# Revit family: Hager-Univers-IP65-D300-H1150-Cl.II-encl-NoHosted-CH-it
name_source: partatom
category: Electrical Equipment
units: mm (PartAtom-declared; Revit-internal decimal feet)

## family parameters
Always vertical = Yes
Cut with Voids When Loaded = No
Panel Configuration = Two Columns, Circuits Across
Part Type = Panelboard
Room Calculation Point = No
Round Connector Dimension = Use Diameter
Shared = No
Work Plane-Based = Yes

## types (6) — shared parameters
Default Elevation = 1219 mm
EF000003 - Tipo di montaggio = EV000384 - A parete
EF000007 - colore = EV000270 - grigio
EF000040 - Altezza = 1150 mm
EF000049 - profondità = 300 mm  [stored 0.984252 ft]
EF000116 - numero RAL = 7035
EF000118 - con piastra di montaggio = No
EF000266 - numero di file = 7
EF001088 - possibilità di applicazione = No
EF001131 - profondità interna = 300 mm  [stored 0.984252 ft]
EF001596 - Attacco Lampada = EV000139 - plastica
EF001613 - Integrità del circuito = EV000494 - senza
EF003532 - adatto per uso esterno = Yes
EF004293 - resistenza agli urti = EV008784 - IK10
EF004464 - tipo di porta = EV002646 - singolo
EF005474 - grado di protezione (IP) = EV006421 - IP65
EF006244 - coperchio/porta trasparente = No
EF006306 - con serratura = Yes
EF007800 - adatto per parafulmine = Yes
EF009170 - spessore materiale scatola = 2 mm  [stored 0.00656168 ft]
EF009171 - spessore materiale porta/coperchio = 2 mm  [stored 0.00656168 ft]
EF009212 - esecuzione coperchio = EV000116 - chiuso
EF015940 - Coprire con rilascio di sovrapressione = No
HG000002 - Con porta = Yes
HG000003 - Gamma = Univers
HG000006 - Ad incasso = No
HG000009 - Porta doppia a battente = No
HG000010 - Porte asimmetriche = No
HG000023 - Custodia a doppia sezione = No
HG000024 - Altezza della sezione inferiore = 600 mm
HG000026 - A pavimento = No
Manufacturer = Hager
Type Comments = Univers
zero-valued in all types: EF000218 - profondità di incasso, EF009554 - numero delle aperture per la piastra della flangia, HG000027 - Altezza dello zoccolo

## per-type parameters (varying)
| type | EF000008 - Larghezza | EF000339 - tipo di copertura | EF000437 - numero di ingressi per conduttori | EF002950 - Numero moduli DIN | EF004427 - numero di moduli | EF008873 - corrente nominale (In) | HG000004 - Codice produttore |
| A parete IP65 L1100 A1150 P300  - FL74S | 1100 mm | EV004216 - porta | 0 | 48 | 336 | 630 A | FL74S |
| A parete IP65 L1100 A1150 P300  - FL74SP | 1100 mm | EV004216 - porta | 0 | 48 | 336 | 630 A | FL74SP |
| A parete IP65 L600 A1150 P300  - FL72S | 600 mm | EV001012 - coperchio | 2 | 24 | 168 | 400 A | FL72S |
| A parete IP65 L600 A1150 P300  - FL72SP | 600 mm | EV001012 - coperchio | 2 | 24 | 168 | 400 A | FL72SP |
| A parete IP65 L850 A1150 P300  - FL73S | 850 mm  [stored 2.78871 ft] | EV001012 - coperchio | 3 | 36 | 252 | 400 A | FL73S |
| A parete IP65 L850 A1150 P300  - FL73SP | 850 mm  [stored 2.78871 ft] | EV001012 - coperchio | 3 | 36 | 252 | 400 A | FL73SP |

note: [stored X ft] marks values corroborated as IEEE doubles in the binary element streams (Revit-internal decimal feet)

## geometry (parser evidence)
native form markers: Blend x4, Sweep x6
no freeform markers — native parametric forms only
